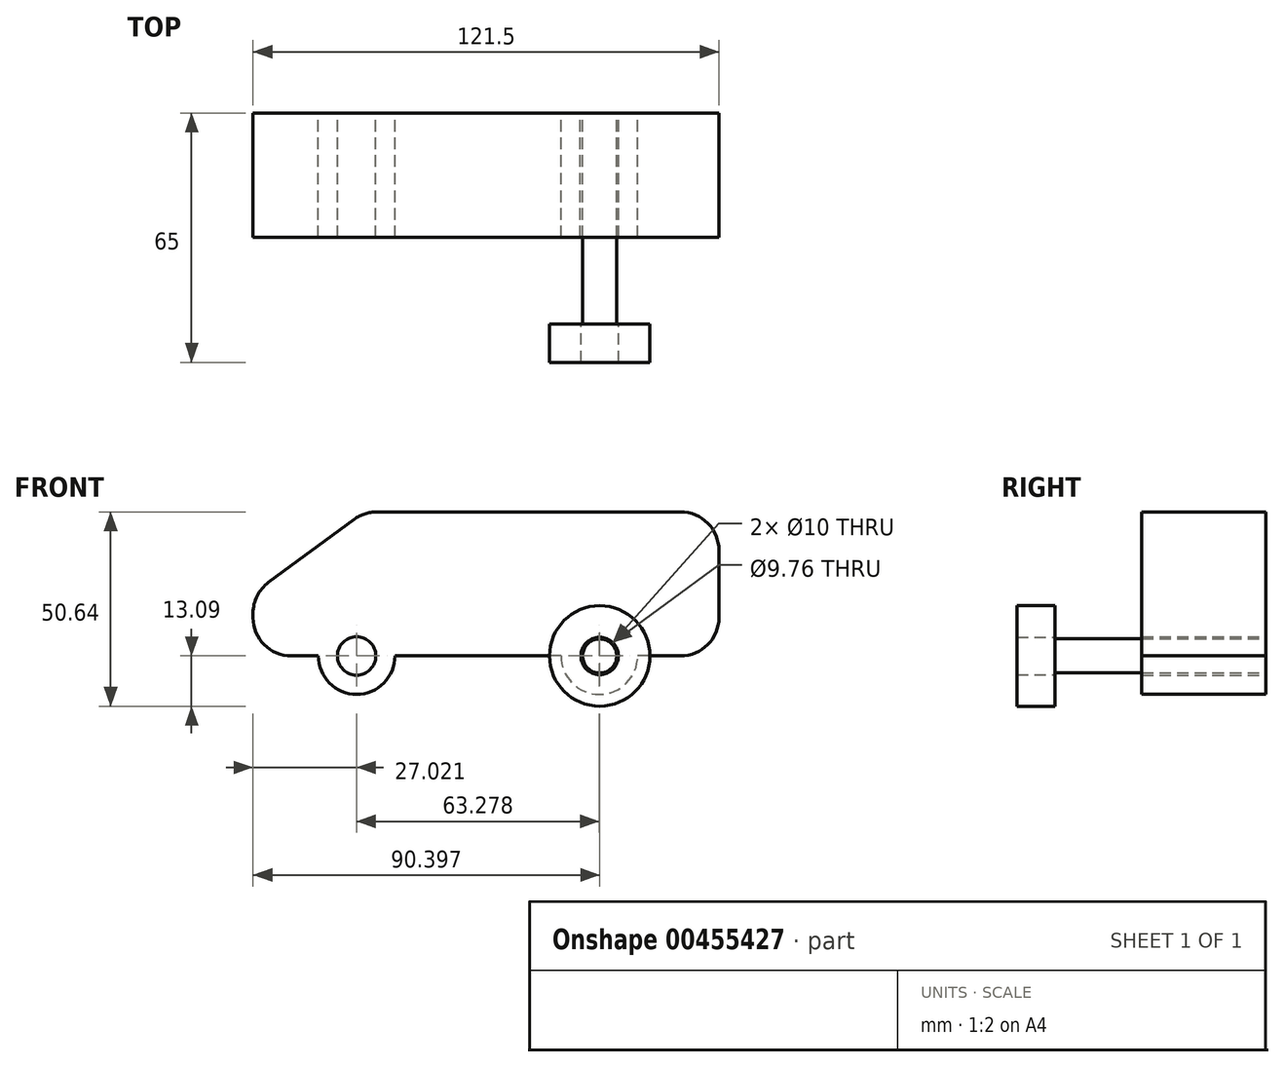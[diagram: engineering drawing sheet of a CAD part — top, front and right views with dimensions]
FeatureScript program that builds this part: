
annotation { "Feature Type Name" : "Feature", "Feature Type Description" : "" }
export const myFeature = defineFeature(function(context is Context, id is Id, definition is map)
    precondition{}
    {
        {
            var Q0;
            Q0=qCreatedBy(makeId("Front.planeOp"),FACE);
            var sketch = newSketch(context, id + "F0", { "sketchPlane" : qUnion([Q0])});
            skLineSegment(sketch, "E0", {"start": v(-54.41, 10) * mm, "end": v(-54.41, 11.13) * mm});
            skLineSegment(sketch, "E1", {"start": v(-50.34, 19.19) * mm, "end": v(-28.01, 35.6) * mm});
            skLineSegment(sketch, "E2", {"start": v(-22.09, 37.55) * mm, "end": v(57.09, 37.55) * mm});
            skLineSegment(sketch, "E3", {"start": v(67.09, 27.55) * mm, "end": v(67.09, 10) * mm});
            skLineSegment(sketch, "E4", {"start": v(57.09, 0) * mm, "end": v(-44.41, 0) * mm});
            skPoint(sketch, "E5.startSnap0", {"position": v(6.34, 0) * mm});
            skCircle(sketch, "E6", {"center": v(-27.39, 0) * mm, "radius": 10 * mm});
            skCircle(sketch, "E7", {"center": v(-27.39, 0) * mm, "radius": 5 * mm});
            skCircle(sketch, "E8", {"center": v(35.89, 0) * mm, "radius": 10 * mm});
            skCircle(sketch, "E9", {"center": v(35.89, 0) * mm, "radius": 5 * mm});
            skPoint(sketch, "E10.visualSharp", {"position": v(67.09, 37.55) * mm});
            skArc(sketch, "E10.filletArc", {"start": v(67.09, 27.55) * mm, "mid": v(64.16, 34.63) * mm, "end": v(57.09, 37.55) * mm});
            skPoint(sketch, "E11.visualSharp", {"position": v(67.09, 0) * mm});
            skArc(sketch, "E11.filletArc", {"start": v(57.09, 0) * mm, "mid": v(64.16, 2.93) * mm, "end": v(67.09, 10) * mm});
            skPoint(sketch, "E12.visualSharp", {"position": v(57.09, 0) * mm});
            skLineSegment(sketch, "E12.filletArc", {"start": v(57.09, 0) * mm, "end": v(57.09, 0) * mm});
            skPoint(sketch, "E13.visualSharp", {"position": v(-54.41, 16.2) * mm});
            skArc(sketch, "E13.filletArc", {"start": v(-50.34, 19.19) * mm, "mid": v(-53.34, 15.65) * mm, "end": v(-54.41, 11.13) * mm});
            skPoint(sketch, "E14.visualSharp", {"position": v(-54.41, 0) * mm});
            skArc(sketch, "E14.filletArc", {"start": v(-54.41, 10) * mm, "mid": v(-51.48, 2.93) * mm, "end": v(-44.41, 0) * mm});
            skPoint(sketch, "E15.visualSharp", {"position": v(-25.37, 37.55) * mm});
            skArc(sketch, "E15.filletArc", {"start": v(-22.09, 37.55) * mm, "mid": v(-25.2, 37.06) * mm, "end": v(-28.01, 35.6) * mm});
            skSolve(sketch);
        }
        {
            var Q0;
            Q0 = qSketchRegion(id + "F0", true);
            extrude(context, id + "F1", {"entities" : qUnion([Q0]), "depth" : 32.4 * mm});
        }
        {
            var Q0;
            Q0=qCreatedBy(makeId("Front.planeOp"),FACE);
            var sketch = newSketch(context, id + "F2", { "sketchPlane" : qUnion([Q0])});
            skCircle(sketch, "E16", {"center": v(35.99, 0) * mm, "radius": 4.45 * mm});
            skSolve(sketch);
        }
        {
            var Q0;
            Q0 = qSketchRegion(id + "F2", true);
            extrude(context, id + "F3", {"entities" : qUnion([Q0]), "depth" : 55 * mm});
        }
        {
            var Q0;
            Q0=makeQuery(id+"F3.opExtrude","CAP_FACE",FACE,{"disambiguationData":[OSD([sQuery(id+"F2.wireOp",EDGE,"E16")])],"isStart":false});
            var sketch = newSketch(context, id + "F4", { "sketchPlane" : qUnion([Q0])});
            skCircle(sketch, "E17", {"center": v(35.99, 0) * mm, "radius": 13.1 * mm});
            skCircle(sketch, "E18", {"center": v(35.99, 0) * mm, "radius": 4.88 * mm});
            skSolve(sketch);
        }
        {
            var Q0;
            Q0 = qSketchRegion(id + "F4", true);
            extrude(context, id + "F5", {"entities" : qUnion([Q0]), "depth" : 10 * mm});
        }
    });
